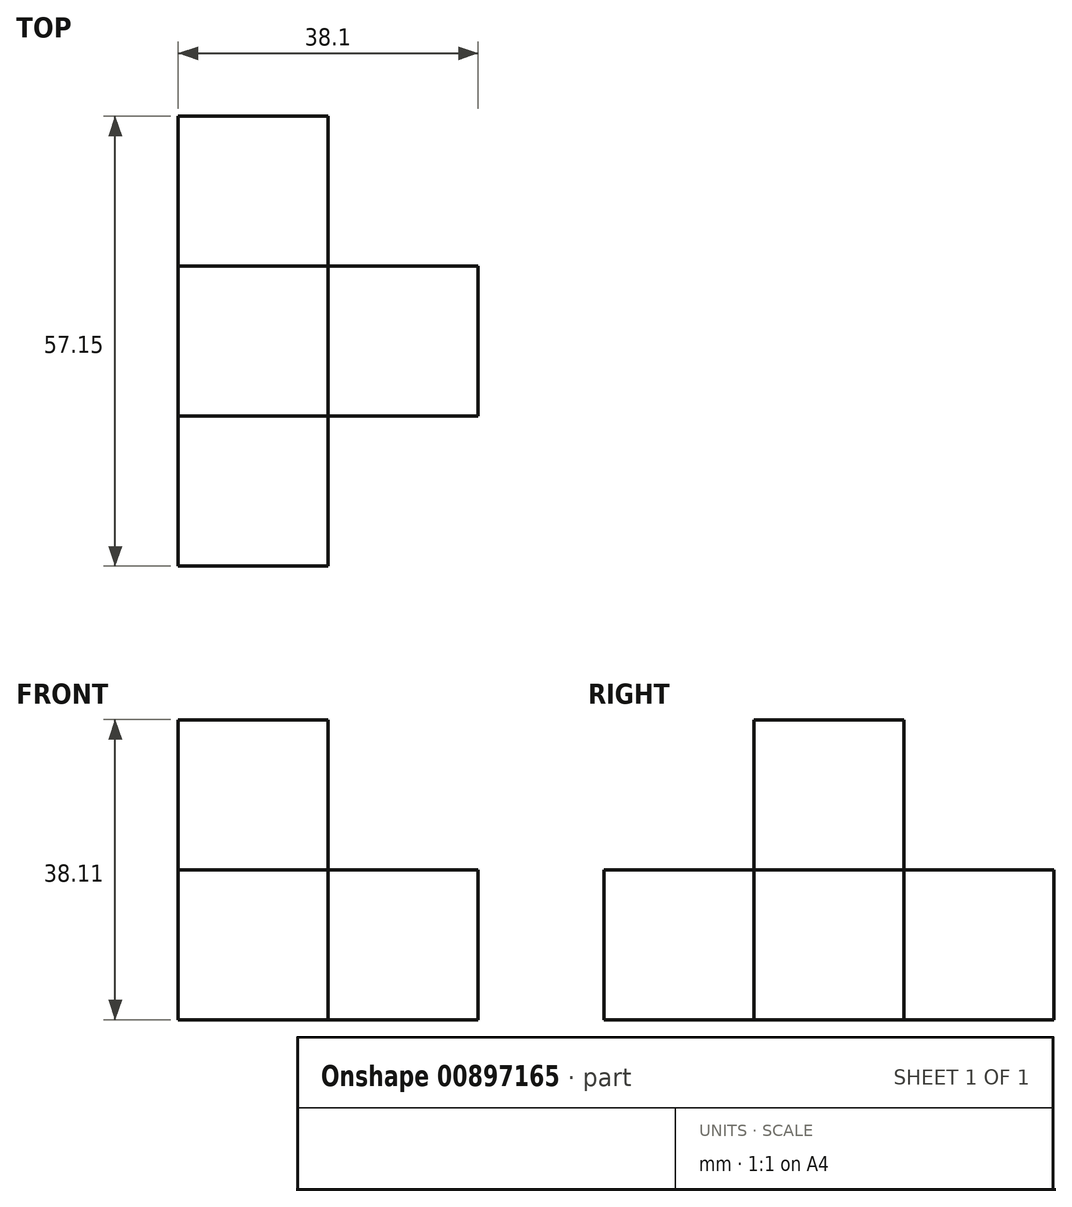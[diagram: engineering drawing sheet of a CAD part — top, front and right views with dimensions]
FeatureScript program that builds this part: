
annotation { "Feature Type Name" : "Feature", "Feature Type Description" : "" }
export const myFeature = defineFeature(function(context is Context, id is Id, definition is map)
    precondition{}
    {
        {
            var Q0;
            Q0=qCreatedBy(makeId("Front.planeOp"),FACE);
            var sketch = newSketch(context, id + "F0", { "sketchPlane" : qUnion([Q0])});
            skLineSegment(sketch, "E0", {"start": v(-41.57, -13.54) * mm, "end": v(-22.52, -13.54) * mm});
            skLineSegment(sketch, "E1", {"start": v(-22.52, -13.54) * mm, "end": v(-22.52, -32.6) * mm});
            skLineSegment(sketch, "E2", {"start": v(-22.52, -32.6) * mm, "end": v(-41.57, -32.6) * mm});
            skLineSegment(sketch, "E3", {"start": v(-41.57, -32.6) * mm, "end": v(-41.57, -13.54) * mm});
            skSolve(sketch);
        }
        {
            var Q0;
            Q0 = qSketchRegion(id + "F0", true);
            extrude(context, id + "F1", {"entities" : qUnion([Q0]), "depth" : 38.1 * mm, "offsetDistance" : 25.4 * mm, "hasSecondDirection" : true, "secondDirectionOppositeDirection" : true, "secondDirectionDepth" : 19.05 * mm});
        }
        {
            var Q0;
            Q0=qCreatedBy(makeId("Top.planeOp"),FACE);
            var sketch = newSketch(context, id + "F2", { "sketchPlane" : qUnion([Q0])});
            skLineSegment(sketch, "E4", {"start": v(-22.51, 0) * mm, "end": v(-41.56, 0) * mm});
            skLineSegment(sketch, "E5", {"start": v(-22.51, 0) * mm, "end": v(-22.51, -19.05) * mm});
            skLineSegment(sketch, "E6", {"start": v(-22.51, -19.05) * mm, "end": v(-41.56, -19.05) * mm});
            skLineSegment(sketch, "E7", {"start": v(-41.56, -19.05) * mm, "end": v(-41.56, 0) * mm});
            skSolve(sketch);
        }
        {
            var Q0;
            Q0 = qSketchRegion(id + "F2", true);
            extrude(context, id + "F3", {"entities" : qUnion([Q0]), "depth" : 19.05 * mm, "offsetDistance" : 25.4 * mm});
        }
        {
            var Q0;
            Q0=makeQuery(id+"F3.opExtrude","SWEPT_BODY",BODY,{"disambiguationData":[OSD([sQuery(id+"F2.wireOp",EDGE,"E4"),sQuery(id+"F2.wireOp",EDGE,"E5"),sQuery(id+"F2.wireOp",EDGE,"E6"),sQuery(id+"F2.wireOp",EDGE,"E7")])]});
            var Q1;
            Q1=qCreatedBy(id+"FbJasmIoojAO0si_2.mateConnectorOp",VERTEX);
            var Q2;
            Q2=qCreatedBy(id+"FHCHLyfXkfHbu53_2.mateConnectorOp",VERTEX);
            transform(context, id + "F4", {"entities" : qUnion([Q0]), "transformType" : TransformType.TRANSLATION_3D, "dx" : 0 * mm, "dy" : 0 * mm, "dz" : -13.54 * mm, "makeCopy" : false});
        }
        {
            var Q0;
            Q0=qCreatedBy(makeId("Right.planeOp"),FACE);
            var sketch = newSketch(context, id + "F5", { "sketchPlane" : qUnion([Q0])});
            skLineSegment(sketch, "E8", {"start": v(-19.05, -13.55) * mm, "end": v(-19.05, -32.6) * mm});
            skLineSegment(sketch, "E9", {"start": v(-19.05, -32.6) * mm, "end": v(0, -32.6) * mm});
            skLineSegment(sketch, "E10", {"start": v(0, -32.6) * mm, "end": v(0, -13.55) * mm});
            skLineSegment(sketch, "E11", {"start": v(0, -13.55) * mm, "end": v(-19.05, -13.55) * mm});
            skSolve(sketch);
        }
        {
            var Q0;
            Q0 = qSketchRegion(id + "F5", true);
            extrude(context, id + "F6", {"entities" : qUnion([Q0]), "depth" : 19.05 * mm, "offsetDistance" : 25.4 * mm});
        }
        {
            var Q0;
            Q0=makeQuery(id+"F6.opExtrude","SWEPT_BODY",BODY,{"disambiguationData":[OSD([sQuery(id+"F5.wireOp",EDGE,"E8"),sQuery(id+"F5.wireOp",EDGE,"E9"),sQuery(id+"F5.wireOp",EDGE,"E10"),sQuery(id+"F5.wireOp",EDGE,"E11")])]});
            transform(context, id + "F7", {"entities" : qUnion([Q0]), "transformType" : TransformType.TRANSLATION_3D, "dx" : -22.52 * mm, "dy" : 0 * mm, "dz" : 0 * mm, "makeCopy" : false});
        }
    });
